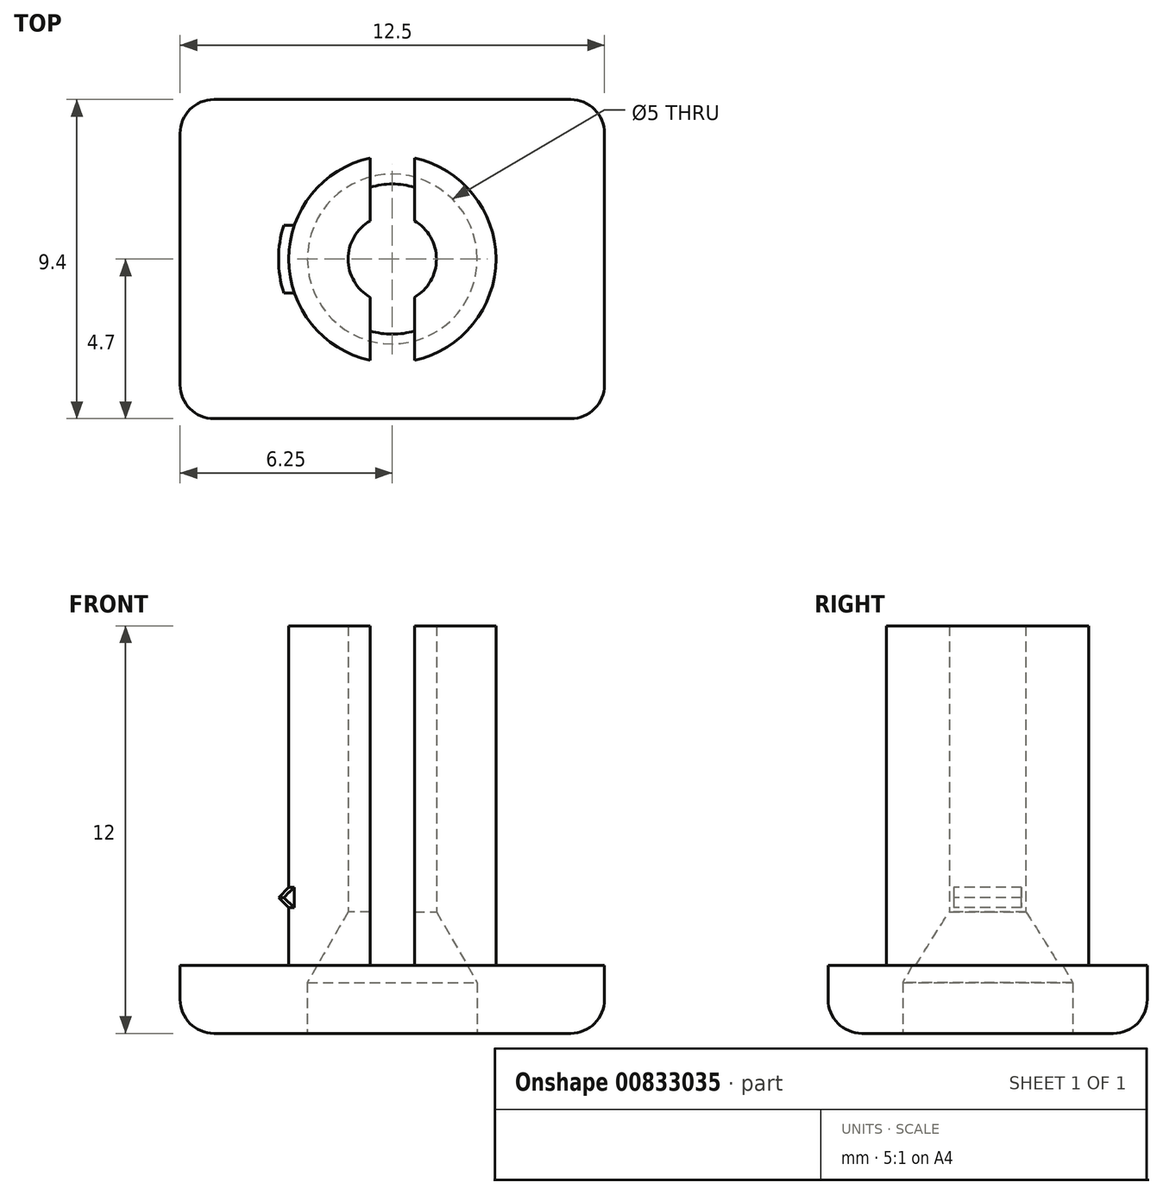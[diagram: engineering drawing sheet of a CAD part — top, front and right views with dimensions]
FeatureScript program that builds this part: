
annotation { "Feature Type Name" : "Feature", "Feature Type Description" : "" }
export const myFeature = defineFeature(function(context is Context, id is Id, definition is map)
    precondition{}
    {
        {
            var Q0;
            Q0=qCreatedBy(makeId("Top.planeOp"),FACE);
            var sketch = newSketch(context, id + "F0", { "sketchPlane" : qUnion([Q0])});
            skLineSegment(sketch, "E0.bottom", {"start": v(-6.25, 4.7) * mm, "end": v(6.25, 4.7) * mm});
            skLineSegment(sketch, "E0.top", {"start": v(-6.25, -4.7) * mm, "end": v(6.25, -4.7) * mm});
            skLineSegment(sketch, "E0.left", {"start": v(-6.25, 4.7) * mm, "end": v(-6.25, -4.7) * mm});
            skLineSegment(sketch, "E0.right", {"start": v(6.25, 4.7) * mm, "end": v(6.25, -4.7) * mm});
            skCircle(sketch, "E1", {"center": v(0, 0) * mm, "radius": 3.05 * mm});
            skSolve(sketch);
        }
        {
            var Q0;
            Q0=makeQuery(id+"F0.imprint","IMPRINT",FACE,{"disambiguationData":[TD([[makeQuery(id+"F0.imprint","IMPRINT",EDGE,{"derivedFrom":sQuery(id+"F0.wireOp",EDGE,"E0.bottom")}),-1.0]])]});
            var Q1;
            Q1=makeQuery(id+"F0.imprint","IMPRINT",FACE,{"disambiguationData":[TD([[makeQuery(id+"F0.imprint","IMPRINT",EDGE,{"derivedFrom":sQuery(id+"F0.wireOp",EDGE,"E1")}),1.0]])]});
            extrude(context, id + "F1", {"entities" : qUnion([Q0, Q1]), "depth" : 2 * mm, "offsetDistance" : 25 * mm});
        }
        {
            var Q0;
            Q0=makeQuery(id+"F0.imprint","IMPRINT",FACE,{"disambiguationData":[TD([[makeQuery(id+"F0.imprint","IMPRINT",EDGE,{"derivedFrom":sQuery(id+"F0.wireOp",EDGE,"E1")}),1.0]])]});
            var Q1;
            Q1=sQuery(id+"F0.wireOp",EDGE,"E1");
            extrude(context, id + "F2", {"entities" : qUnion([Q0]), "operationType" : NewBodyOperationType.ADD, "surfaceOperationType" : NewSurfaceOperationType.ADD, "surfaceEntities" : qUnion([Q1]), "depth" : 12 * mm, "offsetDistance" : 25 * mm});
        }
        {
            var Q0;
            Q0=qCreatedBy(makeId("Front.planeOp"),FACE);
            var sketch = newSketch(context, id + "F3", { "sketchPlane" : qUnion([Q0])});
            skLineSegment(sketch, "E2", {"start": v(0, 12) * mm, "end": v(0, 0) * mm});
            skLineSegment(sketch, "E3", {"start": v(0, 12) * mm, "end": v(-1.3, 12) * mm});
            skLineSegment(sketch, "E4", {"start": v(-1.3, 12) * mm, "end": v(-1.3, 3.58) * mm});
            skLineSegment(sketch, "E5", {"start": v(-1.3, 3.58) * mm, "end": v(-2.5, 1.5) * mm});
            skLineSegment(sketch, "E6", {"start": v(-2.5, 1.5) * mm, "end": v(-2.5, 0) * mm});
            skLineSegment(sketch, "E7", {"start": v(-2.5, 0) * mm, "end": v(0, 0) * mm});
            skLineSegment(sketch, "E8.0", {"start": v(-3.05, 12) * mm, "end": v(3.05, 12) * mm, "construction": true});
            skSolve(sketch);
        }
        {
            var Q0;
            Q0 = qSketchRegion(id + "F3", true);
            var Q1;
            Q1=sQuery(id+"F3.wireOp",EDGE,"E2");
            revolve(context, id + "F4", {"operationType" : NewBodyOperationType.REMOVE, "surfaceOperationType" : NewSurfaceOperationType.NEW, "entities" : qUnion([Q0]), "axis" : qUnion([Q1]), "revolveType" : RevolveType.FULL, "oppositeDirection" : true});
        }
        {
            var Q0;
            Q0=makeQuery(id+"F2.opExtrude","CAP_FACE",FACE,{"disambiguationData":[OSD([sQuery(id+"F0.wireOp",EDGE,"E1")])],"isStart":false});
            var sketch = newSketch(context, id + "F5", { "sketchPlane" : qUnion([Q0])});
            skLineSegment(sketch, "E9.bottom", {"start": v(-0.65, 3.05) * mm, "end": v(0.65, 3.05) * mm});
            skLineSegment(sketch, "E9.top", {"start": v(-0.65, -3.05) * mm, "end": v(0.65, -3.05) * mm});
            skLineSegment(sketch, "E9.left", {"start": v(-0.65, 3.05) * mm, "end": v(-0.65, -3.05) * mm});
            skLineSegment(sketch, "E9.right", {"start": v(0.65, 3.05) * mm, "end": v(0.65, -3.05) * mm});
            skSolve(sketch);
        }
        {
            var Q0;
            Q0 = qSketchRegion(id + "F5", true);
            var Q1;
            Q1=makeQuery(id+"F1.opExtrude","CAP_FACE",FACE,{"disambiguationData":[OSD([sQuery(id+"F0.wireOp",EDGE,"E0.bottom"),sQuery(id+"F0.wireOp",EDGE,"E0.top"),sQuery(id+"F0.wireOp",EDGE,"E0.left"),sQuery(id+"F0.wireOp",EDGE,"E0.right")])],"isStart":false});
            extrude(context, id + "F6", {"entities" : qUnion([Q0]), "operationType" : NewBodyOperationType.REMOVE, "endBound" : BoundingType.UP_TO_SURFACE, "oppositeDirection" : true, "depth" : 25 * mm, "endBoundEntityFace" : qUnion([Q1]), "offsetDistance" : 25 * mm});
        }
        {
            var Q0;
            {var subQ0=sQuery(id+"F0.wireOp",EDGE,"E0.right");var subQ1=sQuery(id+"F0.wireOp",EDGE,"E0.left");var subQ2=sQuery(id+"F0.wireOp",EDGE,"E0.top");var subQ3=sQuery(id+"F0.wireOp",EDGE,"E0.bottom");Q0=makeQuery(id+"F6.boolean.opBoolean","MERGE",FACE,{"derivedFrom":[makeQuery(id+"F1.opExtrude","CAP_FACE",FACE,{"disambiguationData":[OSD([subQ3,subQ2,subQ1,subQ0])],"isStart":false}),makeQuery(id+"F6.opExtrude","CAP_FACE",FACE,{"disambiguationData":[OSD([subQ3,subQ2,subQ1,subQ0])],"isStart":false})]});}
            cPlane(context, id + "F7", {"entities" : qUnion([Q0]), "cplaneType" : CPlaneType.OFFSET, "offset" : 2 * mm, "width" : 150 * mm, "height" : 150 * mm});
        }
        {
            var Q0;
            Q0=qCreatedBy(id+"F7.planeOp",FACE);
            var sketch = newSketch(context, id + "F8", { "sketchPlane" : qUnion([Q0])});
            skArc(sketch, "E10.0", {"start": v(-3.2, 1) * mm, "mid": v(-3.35, 0) * mm, "end": v(-3.2, -1) * mm});
            skLineSegment(sketch, "E11", {"start": v(-3.2, 1) * mm, "end": v(-2.88, 1) * mm});
            skLineSegment(sketch, "E12", {"start": v(-3.2, -1) * mm, "end": v(-2.88, -1) * mm});
            skArc(sketch, "E13.0", {"start": v(-2.88, -1) * mm, "mid": v(-3.05, 0) * mm, "end": v(-2.88, 1) * mm});
            skPoint(sketch, "E14.orphan", {"position": v(-0.65, 2.98) * mm});
            skPoint(sketch, "E15.orphan", {"position": v(-0.65, -2.98) * mm});
            skSolve(sketch);
        }
        {
            var Q0;
            Q0 = qSketchRegion(id + "F8", true);
            extrude(context, id + "F9", {"entities" : qUnion([Q0]), "operationType" : NewBodyOperationType.ADD, "depth" : 0.6 * mm, "offsetDistance" : 25 * mm, "symmetric" : true});
        }
        {
            var Q0;
            Q0=makeQuery(id+"F9.opExtrude","CAP_EDGE",EDGE,{"disambiguationData":[OSD([sQuery(id+"F8.wireOp",EDGE,"E10.0")])],"isStart":false});
            var Q1;
            Q1=makeQuery(id+"F9.opExtrude","CAP_EDGE",EDGE,{"disambiguationData":[OSD([sQuery(id+"F8.wireOp",EDGE,"E10.0")])],"isStart":true});
            chamfer(context, id + "F10", {"entities" : qUnion([Q0, Q1]), "width" : 0.3 * mm, "tangentPropagation" : true});
        }
        {
            var Q0;
            Q0=makeQuery(id+"F1.opExtrude","CAP_EDGE",EDGE,{"disambiguationData":[OSD([sQuery(id+"F0.wireOp",EDGE,"E0.left")])],"isStart":true});
            var Q1;
            Q1=makeQuery(id+"F1.opExtrude","CAP_EDGE",EDGE,{"disambiguationData":[OSD([sQuery(id+"F0.wireOp",EDGE,"E0.top")])],"isStart":true});
            var Q2;
            Q2=makeQuery(id+"F1.opExtrude","CAP_EDGE",EDGE,{"disambiguationData":[OSD([sQuery(id+"F0.wireOp",EDGE,"E0.right")])],"isStart":true});
            var Q3;
            Q3=makeQuery(id+"F1.opExtrude","CAP_EDGE",EDGE,{"disambiguationData":[OSD([sQuery(id+"F0.wireOp",EDGE,"E0.bottom")])],"isStart":true});
            var Q4;
            Q4=makeQuery(id+"F1.opExtrude","SWEPT_EDGE",EDGE,{"disambiguationData":[OSD([sQuery(id+"F0.wireOp",EDGE,"E0.top"),sQuery(id+"F0.wireOp",EDGE,"E0.left")])]});
            var Q5;
            Q5=makeQuery(id+"F1.opExtrude","SWEPT_EDGE",EDGE,{"disambiguationData":[OSD([sQuery(id+"F0.wireOp",EDGE,"E0.top"),sQuery(id+"F0.wireOp",EDGE,"E0.right")])]});
            var Q6;
            Q6=makeQuery(id+"F1.opExtrude","SWEPT_EDGE",EDGE,{"disambiguationData":[OSD([sQuery(id+"F0.wireOp",EDGE,"E0.bottom"),sQuery(id+"F0.wireOp",EDGE,"E0.left")])]});
            var Q7;
            Q7=makeQuery(id+"F1.opExtrude","SWEPT_EDGE",EDGE,{"disambiguationData":[OSD([sQuery(id+"F0.wireOp",EDGE,"E0.bottom"),sQuery(id+"F0.wireOp",EDGE,"E0.right")])]});
            fillet(context, id + "F11", {"entities" : qUnion([Q0, Q1, Q2, Q3, Q4, Q5, Q6, Q7]), "radius" : 1 * mm, "tangentPropagation" : true, "allowEdgeOverflow" : false});
        }
    });
